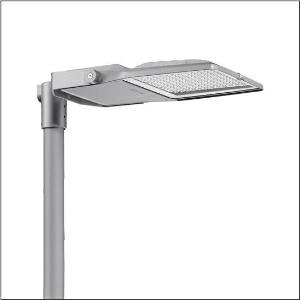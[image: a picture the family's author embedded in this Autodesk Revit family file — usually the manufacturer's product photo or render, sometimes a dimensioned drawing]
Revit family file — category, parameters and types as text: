
# Revit family: floodlight_fl_21_iq_midi___pl64_5xa7782f2e3a_4586
name_source: partatom
category: Lighting Fixtures
units: mm (PartAtom-declared; Revit-internal decimal feet)

## family parameters
Cut with Voids When Loaded = No
Host = Face
Light Source = No
Part Type = Normal
Room Calculation Point = No
Round Connector Dimension = Use Diameter
Shared = No

## types (1)
- --- (1 x LED, 34530 lm, 270.2 W, 3000K)
    Apparent Load = 270 VA
    CIE Flux Codes = 28 80 98 100 100
    Color Rendering = 70
    Color Temperature = 3000K
    Default Elevation = 1800 mm
    Description = Floodlight FL 21 iQ midi, floodlight, primary light control with lens, of PMMA, primary optical cover: protective disc, of toughened safety glass, transparent, light distribution: PL64, light emission: direct distribution, installation type: surface-mounted, LED, High Power LED, rated luminous flux: 34.530lm, luminous efficacy: 128lm/W, light colour: 730, colour temperature: 3000K, control gear: ECG iQ, control: optimised constant luminous flux control (CLO 2.0), Desk-Remote (wireless, voltage-free reading and setting of iQ features in the workshop via application-optimized NFC function/RFID function), Smart-Wire, Night-Set, Temp-Guard, Auto-Match, Street-Remote, with terminal, 6-pole, mains connection: 220..240V, AC, 50/60Hz, start of lifetime: 270W, end of service life: 287W, reduction: 117W, luminaire housing, of diecast aluminium, powder-coated, Siteco® metallic grey (DB 702S), corrosivity category C5 mid according to DIN EN ISO 12944, sealing non-destructively replaceable, please order mast flange separately, mast bracket, of steel, galvanised, powder-coated, Siteco® metallic grey (DB 702S), protection rating (complete): IP66, insulation class (complete): insulation class II (safety insulation), certification: CE, protection symbol: D, impact resistance: IK08, permissible operating ambient temperature: -40..+40°C, permissible operating ambient temperature for outdoor applications: -40..+50°C, standard: DIN EN 12944, LABS conformity tested according to VDMA 24364:2018-05, packaging unit: 1 piece

Light Distribution: PL64
    Height = 76 mm
    Lamp = 1 x LED
    Lamp Light Flux = 34530 lm
    Lamp Power = 270.2 W
    Lamp count = 1
    Length = 657 mm
    Luminous efficacy = 128 lm/W
    Manufacturer = Siteco
    ModVariant = No
    Model = 5XA7782F2E3A
    Number of Poles = 1
    OnlyDefault = Yes
    Power Factor = 1
    Product Name = Floodlight FL 21 iQ midi | PL64
    Product group = floodlight | pylon annexe
    ProductGroupID = 6200
    Protection Class = Protection class II
    Protection Degree = IP 66
    RLX_Detail_Level = 1
    RLX_Emergency_Light_Flux = 0 lm
    RLX_Emergency_Type = 0
    RLX_Emergency_Type_DB = No
    RlxData = <blob elided: 153445 chars, md5=930d2a66>
    Socket = socket
    Standby Power = 0 W
    System Light Flux = 34530 lm
    System Power = 270 W
    Type Comments = factory setting: luminous flux: 100 % | dim-lin: 254 | 620 mA
    Type Image = l_1007123.jpg
    URL = http://relux.com
    VarID = @adj_036805
    Voltage = 0 V
    Weight = 0.00 kg
    Width = 442 mm

## geometry (parser evidence)
native form markers: Blend x4, Sweep x12
no freeform markers — native parametric forms only
